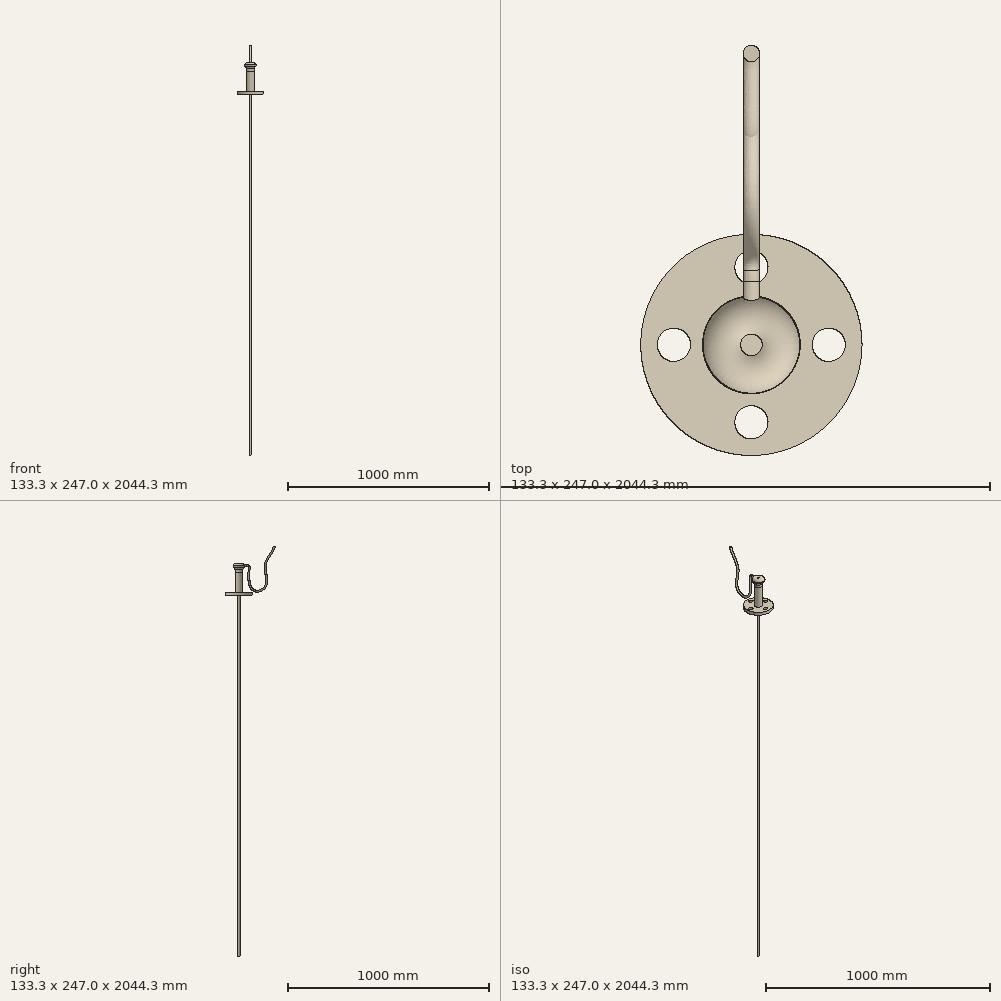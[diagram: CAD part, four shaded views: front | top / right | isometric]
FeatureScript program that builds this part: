
annotation { "Feature Type Name" : "Feature", "Feature Type Description" : "" }
export const myFeature = defineFeature(function(context is Context, id is Id, definition is map)
    precondition{}
    {
        {
            var Q0;
            Q0=qCreatedBy(makeId("Top.planeOp"),FACE);
            var sketch = newSketch(context, id + "F0", { "sketchPlane" : qUnion([Q0])});
            skCircle(sketch, "E0", {"center": v(0, 0) * mm, "radius": 66.65 * mm});
            skSolve(sketch);
        }
        {
            var Q0;
            Q0 = qSketchRegion(id + "F0", true);
            extrude(context, id + "F1", {"entities" : qUnion([Q0]), "depth" : 15 * mm, "offsetDistance" : 25.4 * mm});
        }
        {
            var Q0;
            Q0=makeQuery(id+"F1.opExtrude","CAP_FACE",FACE,{"disambiguationData":[OSD([sQuery(id+"F0.wireOp",EDGE,"E0")])],"isStart":true});
            var sketch = newSketch(context, id + "F2", { "sketchPlane" : qUnion([Q0])});
            skCircle(sketch, "E1", {"center": v(0, 0) * mm, "radius": 6.5 * mm});
            skSolve(sketch);
        }
        {
            var Q0;
            Q0 = qSketchRegion(id + "F2", true);
            extrude(context, id + "F3", {"entities" : qUnion([Q0]), "depth" : 1800 * mm, "offsetDistance" : 25.4 * mm});
        }
        {
            var Q0;
            Q0=makeQuery(id+"F1.opExtrude","CAP_FACE",FACE,{"disambiguationData":[OSD([sQuery(id+"F0.wireOp",EDGE,"E0")])],"isStart":false});
            var sketch = newSketch(context, id + "F4", { "sketchPlane" : qUnion([Q0])});
            skCircle(sketch, "E2", {"center": v(0, 0) * mm, "radius": 46.65 * mm, "construction": true});
            skCircle(sketch, "E3", {"center": v(46.65, 0) * mm, "radius": 10 * mm});
            skCircle(sketch, "E4.1.1", {"center": v(0, 46.65) * mm, "radius": 10 * mm});
            skCircle(sketch, "E4.2.1", {"center": v(-46.65, 0) * mm, "radius": 10 * mm});
            skCircle(sketch, "E4.3.1", {"center": v(0, -46.65) * mm, "radius": 10 * mm});
            skSolve(sketch);
        }
        {
            var Q0;
            Q0 = qSketchRegion(id + "F4", true);
            extrude(context, id + "F5", {"entities" : qUnion([Q0]), "operationType" : NewBodyOperationType.REMOVE, "endBound" : BoundingType.UP_TO_NEXT, "oppositeDirection" : true, "depth" : 25.4 * mm, "offsetDistance" : 25.4 * mm});
        }
        {
            var Q0;
            Q0=makeQuery(id+"F1.opExtrude","CAP_FACE",FACE,{"disambiguationData":[OSD([sQuery(id+"F0.wireOp",EDGE,"E0")])],"isStart":false});
            var sketch = newSketch(context, id + "F6", { "sketchPlane" : qUnion([Q0])});
            skCircle(sketch, "E5", {"center": v(0, 0) * mm, "radius": 19.25 * mm});
            skSolve(sketch);
        }
        {
            var Q0;
            Q0 = qSketchRegion(id + "F6", true);
            extrude(context, id + "F7", {"entities" : qUnion([Q0]), "operationType" : NewBodyOperationType.ADD, "depth" : 100 * mm, "offsetDistance" : 25.4 * mm});
        }
        {
            var Q0;
            Q0=qCreatedBy(makeId("Right.planeOp"),FACE);
            var sketch = newSketch(context, id + "F8", { "sketchPlane" : qUnion([Q0])});
            skLineSegment(sketch, "E6", {"start": v(0, 230) * mm, "end": v(0, 0) * mm, "construction": true});
            skArc(sketch, "E7", {"start": v(0, 143.68) * mm, "mid": v(-12.83, 158.37) * mm, "end": v(-29.11, 147.63) * mm});
            skPoint(sketch, "E8.visualSharp", {"position": v(-29.65, 143.68) * mm});
            skArc(sketch, "E8.filletArc", {"start": v(-29.11, 147.63) * mm, "mid": v(-29.47, 144.57) * mm, "end": v(-28.87, 141.55) * mm});
            skLineSegment(sketch, "E9", {"start": v(0, 143.68) * mm, "end": v(0, 115) * mm});
            skLineSegment(sketch, "E10", {"start": v(0, 115) * mm, "end": v(-19.21, 115) * mm});
            skLineSegment(sketch, "E11", {"start": v(-28.87, 141.55) * mm, "end": v(-26.57, 139.67) * mm});
            skLineSegment(sketch, "E12", {"start": v(-19.21, 128.43) * mm, "end": v(-19.21, 115) * mm});
            skPoint(sketch, "E13.newPointA", {"position": v(-19.37, 133.8) * mm});
            skLineSegment(sketch, "E14", {"start": v(-19.21, 128.43) * mm, "end": v(-26.57, 139.67) * mm});
            skSolve(sketch);
        }
        {
            var Q0;
            Q0 = qSketchRegion(id + "F8", true);
            var Q1;
            Q1=sQuery(id+"F8.wireOp",EDGE,"E6");
            revolve(context, id + "F9", {"operationType" : NewBodyOperationType.ADD, "surfaceOperationType" : NewSurfaceOperationType.NEW, "entities" : qUnion([Q0]), "axis" : qUnion([Q1]), "revolveType" : RevolveType.FULL});
        }
        {
            var Q0;
            Q0=qCreatedBy(makeId("Top.planeOp"),FACE);
            cPlane(context, id + "F10", {"entities" : qUnion([Q0]), "cplaneType" : CPlaneType.OFFSET, "offset" : 160.02 * mm, "width" : 152.4 * mm, "height" : 152.4 * mm});
        }
        {
            var Q0;
            Q0=qCreatedBy(id+"F10.planeOp",FACE);
            var sketch = newSketch(context, id + "F11", { "sketchPlane" : qUnion([Q0])});
            skCircle(sketch, "E15", {"center": v(0, 0) * mm, "radius": 6.5 * mm});
            skSolve(sketch);
        }
        {
            var Q0;
            Q0 = qSketchRegion(id + "F11", true);
            extrude(context, id + "F12", {"entities" : qUnion([Q0]), "operationType" : NewBodyOperationType.REMOVE, "oppositeDirection" : true, "depth" : 154.7 * mm, "offsetDistance" : 25.4 * mm});
        }
        {
            var Q0;
            Q0=qCreatedBy(makeId("Front.planeOp"),FACE);
            cPlane(context, id + "F13", {"entities" : qUnion([Q0]), "cplaneType" : CPlaneType.OFFSET, "offset" : 25.4 * mm, "oppositeDirection" : true, "width" : 152.4 * mm, "height" : 152.4 * mm});
        }
        {
            var Q0;
            Q0=qCreatedBy(id+"F13.planeOp",FACE);
            var sketch = newSketch(context, id + "F14", { "sketchPlane" : qUnion([Q0])});
            skCircle(sketch, "E16", {"center": v(0, 147.63) * mm, "radius": 5 * mm});
            skSolve(sketch);
        }
        {
            var Q0;
            Q0 = qSketchRegion(id + "F14", true);
            extrude(context, id + "F15", {"entities" : qUnion([Q0]), "operationType" : NewBodyOperationType.ADD, "oppositeDirection" : true, "depth" : 12.7 * mm, "offsetDistance" : 25.4 * mm});
        }
        {
            var Q0;
            Q0=makeQuery(id+"F15.opExtrude","CAP_EDGE",EDGE,{"disambiguationData":[OSD([sQuery(id+"F14.wireOp",EDGE,"E16")])],"isStart":false});
            cPlane(context, id + "F16", {"entities" : qUnion([Q0]), "cplaneType" : CPlaneType.LINE_ANGLE, "offset" : 25.4 * mm, "angle" : 90 * degree, "oppositeDirection" : true, "width" : 152.4 * mm, "height" : 152.4 * mm});
        }
        {
            var Q0;
            Q0=qCreatedBy(id+"F16.planeOp",FACE);
            var sketch = newSketch(context, id + "F17", { "sketchPlane" : qUnion([Q0])});
            skFitSpline(sketch, "E17", {"points": [v(-38.1, 147.53) * mm, v(-43.6, 147.53) * mm, v(-46.9, 147.32) * mm, v(-49.78, 141.82) * mm, v(-49.85, 136.8) * mm, v(-48.83, 83.64) * mm, v(-57, 43.18) * mm, v(-81.13, 22.95) * mm, v(-112.64, 26.06) * mm, v(-137.54, 59.52) * mm, v(-130.15, 139.67) * mm, v(-147.51, 189.18) * mm, v(-170.86, 227.3) * mm, v(-175.52, 243.65) * mm], "startDerivative": vector(-150.31, -7.82) * mm, "endDerivative": vector(-43.26, 243.48) * mm});
            skSolve(sketch);
        }
        {
            var Q0;
            Q0=makeQuery(id+"F15.opExtrude","CAP_FACE",FACE,{"disambiguationData":[OSD([sQuery(id+"F14.wireOp",EDGE,"E16")])],"isStart":false});
            var Q1;
            Q1=sQuery(id+"F17.wireOp",EDGE,"E17");
            sweep(context, id + "F18", {"operationType" : NewBodyOperationType.ADD, "profiles" : qUnion([Q0]), "path" : qUnion([Q1])});
        }
    });
